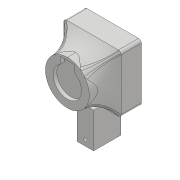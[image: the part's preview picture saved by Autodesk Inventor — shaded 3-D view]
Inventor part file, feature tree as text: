
AUTODESK INVENTOR PART (.ipt)
format: ipt  version: 2018 (Build 220112000, 112)  size: 749,568 bytes
history: native  units: mm
features: sketch x33, extrude x29, projected_geometry x29, fillet x4, hole x3, chamfer x1, mirror x1, revolve x1
ambient origin geometry x8: Origin, YZ Plane, XZ Plane, XY Plane, X Axis, Y Axis, Z Axis, Center Point
bodies: Solid1 (feature_tree)
feature tree (101):
  extrude  "Extrusion1"  Depth=45.0mm
  extrude  "Extrusion2"  Depth=2.25mm
  hole  "Hole1"  [1 undecoded]
  hole  "Hole2"  [1 undecoded]
  fillet  "Fillet1"  Radius=14.0mm
  extrude  "Extrusion3"  Depth=18.5mm
  extrude  "Extrusion4"  Depth=10.0mm
  extrude  "Extrusion5"  Depth=2.195mm
  extrude  "Extrusion6"  Depth=20.5mm
  hole  "Hole3"  [1 undecoded]
  extrude  "Extrusion7"  Depth=0.5mm
  extrude  "Extrusion8"  Depth=5.0mm TaperAngle=0.0deg
  extrude  "Extrusion9"  Depth=10.0mm
  extrude  "Extrusion10"  Depth=10.0mm
  extrude  "Extrusion11"  Depth=14.5mm
  extrude  "Extrusion12"  Depth=14.5mm
  extrude  "Extrusion13"  Depth=5.0mm
  extrude  "Extrusion14"  Depth=2.25mm
  extrude  "Extrusion15"  Depth=5.0mm
  extrude  "Extrusion16"  Depth=9.0mm
  extrude  "Extrusion17"  Depth=4.0mm
  chamfer  "Chamfer1"  Distance=1.0mm
  fillet  "Fillet8"  Radius=20.7mm
  mirror  "Mirror1"
  extrude  "Extrusion18"  Depth=32.0mm
  extrude  "Extrusion19"  Depth=1.0mm TaperAngle=0.0deg
  extrude  "Extrusion20"  Depth=8.0mm
  extrude  "Extrusion21"  Depth=0.2mm TaperAngle=0.0deg
  extrude  "Extrusion22"  Depth=0.5mm TaperAngle=0.0deg
  extrude  "Extrusion23"  Depth=3.0mm TaperAngle=0.0deg
  extrude  "Extrusion24"  Depth=0.2mm TaperAngle=0.0deg
  sketch  "Sketch35"  dims[d91=8.0mm d92=0.0mm d93=3.0mm d94=0.0mm]
  revolve  "Revolution1"  Angle=45.0deg
  extrude  "Extrusion25"  Depth=22.55mm TaperAngle=0.0deg
  fillet  "Fillet11"  Radius=4.0mm
  fillet  "Fillet14"  Radius=4.0mm
  extrude  "Extrusion33"  Depth=52.1mm
  extrude  "Extrusion34"  Depth=30.0mm
  extrude  "Extrusion35"  Depth=30.0mm
  extrude  "Extrusion36"  Depth=30.0mm
  sketch  "Sketch1"  dims[d0=24.5mm d1=45.0mm]
  sketch  "Sketch2"  dims[d2=1.95mm d3=0.0mm d4=2.25mm]
  projected_geometry  "Projected Loop1"
  sketch  "Sketch3"  dims[d5=20.0mm d6=2.25mm]
  projected_geometry  "Projected Loop2"
  sketch  "Sketch4"  dims[d7=5.25mm d8=5.25mm d9=14.0mm]
  projected_geometry  "Projected Loop3"
  sketch  "Sketch5"  dims[d10=5.25mm d11=18.5mm]
  projected_geometry  "Projected Loop4"
  sketch  "Sketch6"  dims[d12=10.0mm d13=0.0mm d14=20.5mm]
  projected_geometry  "Projected Loop5"
  sketch  "Sketch7"  dims[d15=2.0mm d16=2.195mm]
  projected_geometry  "Projected Loop6"
  sketch  "Sketch8"  dims[d17=2.0mm]
  projected_geometry  "Projected Loop7"
  sketch  "Sketch9"  dims[d18=2.4mm d19=6.0mm d20=4.4mm d21=2.0mm d22=90.0deg d23=8.0mm d24=20.594885mm d25=20.5mm]
  projected_geometry  "Projected Loop8"
  projected_geometry  "Projected Loop9"
  sketch  "Sketch10"  dims[d26=26.65mm d27=2.0mm]
  projected_geometry  "Projected Loop10"
  projected_geometry  "Projected Loop11"
  sketch  "Sketch11"  dims[d28=2.0mm]
  projected_geometry  "Projected Loop12"
  sketch  "Sketch12"  dims[d29=2.4mm d30=6.0mm d31=4.4mm d32=2.0mm d33=90.0deg d34=8.0mm d35=20.594885mm d36=0.5mm]
  sketch  "Sketch13"  dims[d37=18.0mm d38=5.0mm d39=0.0mm]
  sketch  "Sketch14"  dims[d41=10.0mm d42=0.0mm d43=24.5mm]
  projected_geometry  "Projected Loop13"
  sketch  "Sketch15"  dims[d44=1.15mm d45=0.0mm d46=10.0mm]
  sketch  "Sketch16"  dims[d47=21.0mm d48=14.5mm]
  projected_geometry  "Projected Loop14"
  sketch  "Sketch17"  dims[d49=20.0mm d50=14.5mm]
  projected_geometry  "Projected Loop15"
  sketch  "Sketch18"  dims[d51=24.5mm d52=5.0mm]
  projected_geometry  "Projected Loop16"
  sketch  "Sketch19"  dims[d53=5.0mm d54=2.25mm]
  projected_geometry  "Projected Loop17"
  sketch  "Sketch20"  dims[d55=2.25mm d56=5.0mm]
  projected_geometry  "Projected Loop18"
  sketch  "Sketch22"  dims[d57=5.0mm d58=9.0mm]
  sketch  "Sketch25"  dims[d59=14.75mm d60=4.0mm d61=1.0mm d62=0.0mm d63=20.7mm]
  sketch  "Sketch27"  dims[d64=2.4mm d65=6.0mm d66=4.4mm d67=2.0mm d68=90.0deg d69=8.0mm d70=20.594885mm d72=32.0mm]
  projected_geometry  "Projected Loop22"
  sketch  "Sketch28"  dims[d73=5.0mm d74=0.0mm d75=1.0mm d76=0.0mm]
  projected_geometry  "Projected Loop23"
  sketch  "Sketch29"  dims[d77=12.25mm d78=0.0mm d80=8.0mm]
  projected_geometry  "Projected Loop24"
  sketch  "Sketch30"  dims[d81=4.5mm d82=0.0mm d84=0.2mm d85=0.0mm]
  projected_geometry  "Projected Loop25"
  sketch  "Sketch33"  dims[d86=21.0mm d87=0.5mm d88=0.0mm]
  projected_geometry  "Projected Loop26"
  sketch  "Sketch36"  dims[d95=5.0mm d96=0.0mm d98=0.2mm d99=0.0mm]
  projected_geometry  "Projected Loop27"
  sketch  "Sketch45"  dims[d100=0.2mm d101=0.0mm d102=2.5mm d103=2.0mm d104=45.0deg]
  projected_geometry  "Projected Loop39"
  sketch  "Sketch46"  dims[d114=0.5mm d115=22.55mm d116=0.0mm d128=4.0mm d129=0.0mm d130=4.0mm d131=0.0mm]
  projected_geometry  "Projected Loop40"
  sketch  "Sketch47"  dims[d132=19.2mm d133=0.0mm d134=52.1mm]
  projected_geometry  "Projected Loop41"
  sketch  "Sketch48"  dims[d135=6.8mm d136=0.0mm d137=9.0mm d138=9.0mm d139=25.0mm d140=6.9mm d141=0.0mm d142=5.2mm d143=5.2mm d144=5.2mm d145=5.2mm d146=2.5mm d147=0.0mm d148=5.0mm d149=90.0deg d150=5.0mm d151=105.0mm d152=105.0mm d153=5.0mm d154=0.0mm d191=5.1mm d194=50.0mm d226=10.0mm d227=0.0mm d228=28.0mm d229=32.0mm d230=0.0mm d231=30.0mm d232=117.3mm d233=50.0mm d234=0.0mm d235=6.0mm d236=10.3mm d237=60.0mm d238=0.0mm]
  projected_geometry  "Projected Loop42"
  projected_geometry  "Project Cut Edges1"
note: 3 required parameter values undecoded (feature->parameter linkage not recoverable at this tier; creation-order binding heuristic only, values carry confidence <= 0.55)
